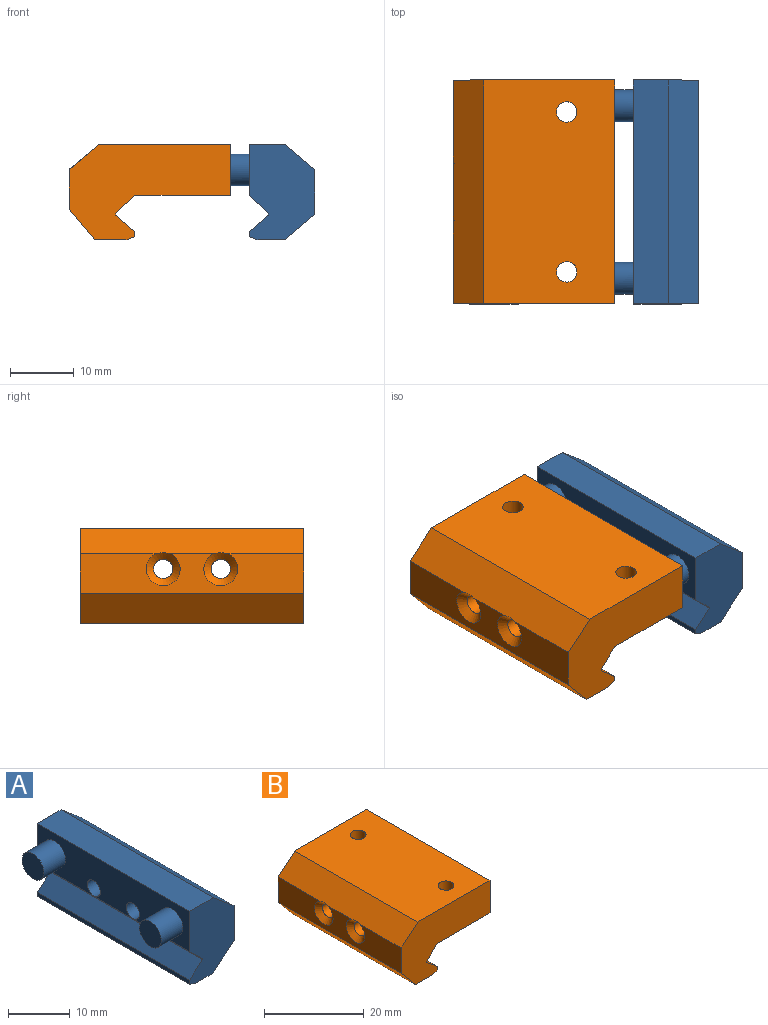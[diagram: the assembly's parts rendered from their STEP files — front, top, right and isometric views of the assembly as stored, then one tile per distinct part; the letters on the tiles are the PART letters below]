
ASSEMBLY  parts=2 mates=1
PART A: 19 faces, bbox 15.3x35x15 mm
  f0: plane 35x5.48mm, normal (0,0,1), area 191.9mm2, adj f2,f3,f5,f11
  f1: plane 35x0.8mm, normal (-1,0,0), area 28mm2, adj f2,f3,f8,f16
  f2: plane 15x10.25mm, normal (0,1,0), area 125.5mm2, adj f0,f1,f4,f5,f6,f7,f8,f9
  f3: plane 15x10.25mm, normal (0,-1,0), area 125.5mm2, adj f0,f1,f4,f5,f6,f7,f8,f9
  f4: plane 35x7mm, normal (1,0,0), area 230.9mm2, adj f2,f3,f5,f7,f17,f18
  f5: plane 35x4.77mm, normal (0.64,0,0.77), area 217.8mm2, adj f0,f2,f3,f4
  f6: plane 35x4.11mm, normal (0,0,-1), area 143.8mm2, adj f2,f3,f7,f16
  f7: plane 35x4.77mm, normal (0.64,0,-0.77), area 217.8mm2, adj f2,f3,f4,f6
  f8: plane 35x3mm, normal (-0.65,0,0.76), area 138.9mm2, adj f1,f2,f3,f10
  f9: plane 35x3mm, normal (-0.7,0,-0.72), area 146mm2, adj f2,f3,f10,f11
  f10: plane 35x0.2mm, normal (-1,0,0), area 7mm2, adj f2,f3,f8,f9
  f11: plane 35x8mm, normal (-1,0,0), area 226.6mm2, adj f0,f2,f3,f9,f12,f14,f17,f18
  f12: cylinder r=2.5mm len=5mm, axis (1,0,0), area 78.5mm2, adj f11,f13
  f13: plane 5x5mm, normal (-1,0,0), area 19.6mm2, adj f12
  f14: cylinder r=2.5mm len=5mm, axis (1,0,0), area 78.5mm2, adj f11,f15
  f15: plane 5x5mm, normal (-1,0,0), area 19.6mm2, adj f14
  f16: plane 35x1.37mm, normal (-0.34,0,-0.94), area 51.2mm2, adj f1,f2,f3,f6
  f17: cylinder r=1.5mm len=10.25mm, axis (-1,0,0), area 96.6mm2, adj f4,f11
  f18: cylinder r=1.5mm len=10.25mm, axis (-1,0,0), area 96.6mm2, adj f4,f11
PART B: 24 faces, bbox 25.3x35x15 mm
  f0: plane 25.25x15mm, normal (0,-1,0), area 245.5mm2, adj f2,f3,f4,f7,f8,f9,f10,f11
  f1: plane 25.25x15mm, normal (0,1,0), area 245.5mm2, adj f2,f3,f4,f7,f8,f9,f10,f11
  f2: plane 35x0.8mm, normal (1,0,0), area 28mm2, adj f0,f1,f12,f19
  f3: plane 35x15mm, normal (0,0,-1), area 508.9mm2, adj f0,f1,f5,f6,f11,f14
  f4: plane 35x6.23mm, normal (-1,0,0), area 174.8mm2, adj f0,f1,f8,f10,f22,f23
  f5: cylinder r=1.6mm len=8mm, axis (0,0,-1), area 80.4mm2, adj f3,f7
  f6: cylinder r=1.6mm len=8mm, axis (0,0,-1), area 80.4mm2, adj f3,f7
  f7: plane 35x20.48mm, normal (0,0,1), area 700.8mm2, adj f0,f1,f5,f6,f8,f14
  f8: plane 35x4.77mm, normal (-0.64,0,0.77), area 217.3mm2, adj f0,f1,f4,f7,f22,f23
  f9: plane 35x4.88mm, normal (0,0,-1), area 170.7mm2, adj f0,f1,f10,f19
  f10: plane 35x4.77mm, normal (-0.77,0,-0.64), area 217.8mm2, adj f0,f1,f4,f9
  f11: plane 35x3mm, normal (0.7,0,-0.72), area 146mm2, adj f0,f1,f3,f13
  f12: plane 35x3mm, normal (0.65,0,0.76), area 138.9mm2, adj f0,f1,f2,f13
  f13: plane 35x0.2mm, normal (1,0,0), area 7mm2, adj f0,f1,f11,f12
  f14: plane 35x8mm, normal (1,0,0), area 225mm2, adj f0,f1,f3,f7,f15,f17,f20,f21
  f15: cylinder r=2.55mm len=5.1mm, axis (1,0,0), area 81.7mm2, adj f14,f16
  f16: plane 5.1x5.1mm, normal (1,0,0), area 20.4mm2, adj f15
  f17: cylinder r=2.55mm len=5.1mm, axis (1,0,0), area 81.7mm2, adj f14,f18
  f18: plane 5.1x5.1mm, normal (1,0,0), area 20.4mm2, adj f17
  f19: plane 35x1.37mm, normal (0.34,0,-0.94), area 51.2mm2, adj f0,f1,f2,f9
  f20: cylinder r=1.5mm len=24.1mm, axis (1,0,0), area 227.1mm2, adj f14,f22
  f21: cylinder r=1.5mm len=24.1mm, axis (1,0,0), area 227.1mm2, adj f14,f23
  f22: cone r=1.5mm half-angle=45deg, axis (-1,0,0), area 20.9mm2, adj f4,f8,f20
  f23: cone r=1.5mm half-angle=45deg, axis (-1,0,0), area 20.9mm2, adj f4,f8,f21
PLACE A t=(-13.7,-80.85,-44.36)mm
PLACE B t=(-16.6,-80.85,-44.36)mm
MATE slider A.f18 <-> B.f20  axis (-1,0,0) through (-6.2,-76.35,-42.76)mm
